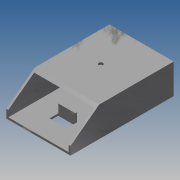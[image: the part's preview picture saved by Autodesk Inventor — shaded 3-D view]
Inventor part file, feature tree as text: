
AUTODESK INVENTOR PART (.ipt)
format: ipt  version: 2014 SP1 (Build 180222100, 222)  size: 139,776 bytes
history: native  units: in
note: dims shown in document units (in); Inventor stores cm internally (conversion verified against a paired STEP export)
features: sketch x6, extrude x4, hole x2, plane x1
ambient origin geometry x8: Origin, YZ Plane, XZ Plane, XY Plane, X Axis, Y Axis, Z Axis, Center Point
bodies: Solid1 (feature_tree)
feature tree (13):
  extrude  "Extrusion1"  Depth=1.5in
  plane  "Work Plane1"
  extrude  "Extrusion2"  Depth=6.0in TaperAngle=0.0deg
  extrude  "Extrusion4"  Depth=1.0in TaperAngle=0.0deg
  extrude  "Extrusion5"  Depth=1.0in
  hole  "holePair"  [1 undecoded]
  hole  "Hole5"  [1 undecoded]
  sketch  "Sketch1"  dims[d0=3.5in d1=1.5in]
  sketch  "Sketch2"  dims[d2=0.12in d3=6.0in d4=0.0in]
  sketch  "Sketch5"  dims[d5=-0.2542in d6=1.0in d7=0.0in]
  sketch  "Sketch7"  dims[d8=5.0in d21=1.0in]
  sketch  "Sketch9"  dims[d22=0.1in d23=1.75in]
  sketch  "Sketch10"  dims[d24=1.25in d25=0.5in d26=0.0in d36=0.5in d37=1.0in d38=0.0in d39=1.0in d40=0.0in d59=0.25in d60=0.75in d61=0.75in d62=0.25in d63=2.0in d67=0.25in d68=0.75in d69=0.375in d70=0.25in d71=0.5635in d72=1.0in d73=0.8108in d74=1.5in d75=0.25in d76=0.75in d77=0.375in d78=0.25in d79=0.5635in d80=1.0in d81=0.8108in]
note: 2 required parameter values undecoded (feature->parameter linkage not recoverable at this tier; creation-order binding heuristic only, values carry confidence <= 0.55)
